# Revit family: Faucet-Lavatory-KOHLER-ALEO-K-72275T
name_source: partatom
category: Plumbing Fixtures
revit_build: Autodesk Revit 2017 (Build: 20160225_1515(x64)
units: mm (PartAtom-declared; Revit-internal decimal feet)

## family parameters
Cut with Voids When Loaded = No
Host = Face
OmniClass Number = 23.31.11.00
OmniClass Title = Faucets
Part Type = Normal
Room Calculation Point = No
Round Connector Dimension = Use Diameter
Shared = No

## types (3) — shared parameters
ADA Compliant = No
Assembly Code = D2010
CW Connection = Yes
Cold Water Inlet = Cold Water Inlet
Date Modified = 09/08/2020
Default Elevation = 36"
Finish = Kohler-Metal-CP-Polished_Chrome
HW Connection = Yes
Handle Clearance = 3 9/16"
Height = 5 9/16"
Hot Water Inlet = Hot Water Inlet
Length = 3 15/16"
Manufacturer = KOHLER Co.
Master Format 2014 = 22 41 39
Master Format 2014 Name = Residential Faucets, Supplies, and Trim
Material = Premium Metal Construction
Product Name = Aleo
Spout Reach = 3 15/16"
URL = http://www.kohler.com.cn
Vent Connection = No
Waste Connection = No
Waste Water Outlet = Waste Water Outlet
WaterSense Certified = No
Width = 2"

## per-type parameters (varying)
| type | Description | Drain Included | Flow Rate | Hot Water Inlet Dia | Model | Pressure | Tow Connector | Type |
| Cold Water Inlet, CP-Polished Chrome | COLD WATER LAVATORY FAUCET | No | 2 GPM | 0" | K-72275T-4CD-CP | 45.00 psi | No | 3 |
| Without Drain, CP-Polished Chrome | SINGLE LEVER LAV MIXER | No | 2 GPM | 1/2" | K-72275T-4ND-CP | 45.00 psi | Yes | 2 |
| CP-Polished Chrome | SINGLE HANDLE LAVATORY FAUCET | Yes | 1 GPM | 1/2" | K-72275T-4E2-CP | 60.00 psi | Yes | 1 |

## geometry (parser evidence)
native form markers: Sweep x5
no freeform markers — native parametric forms only
